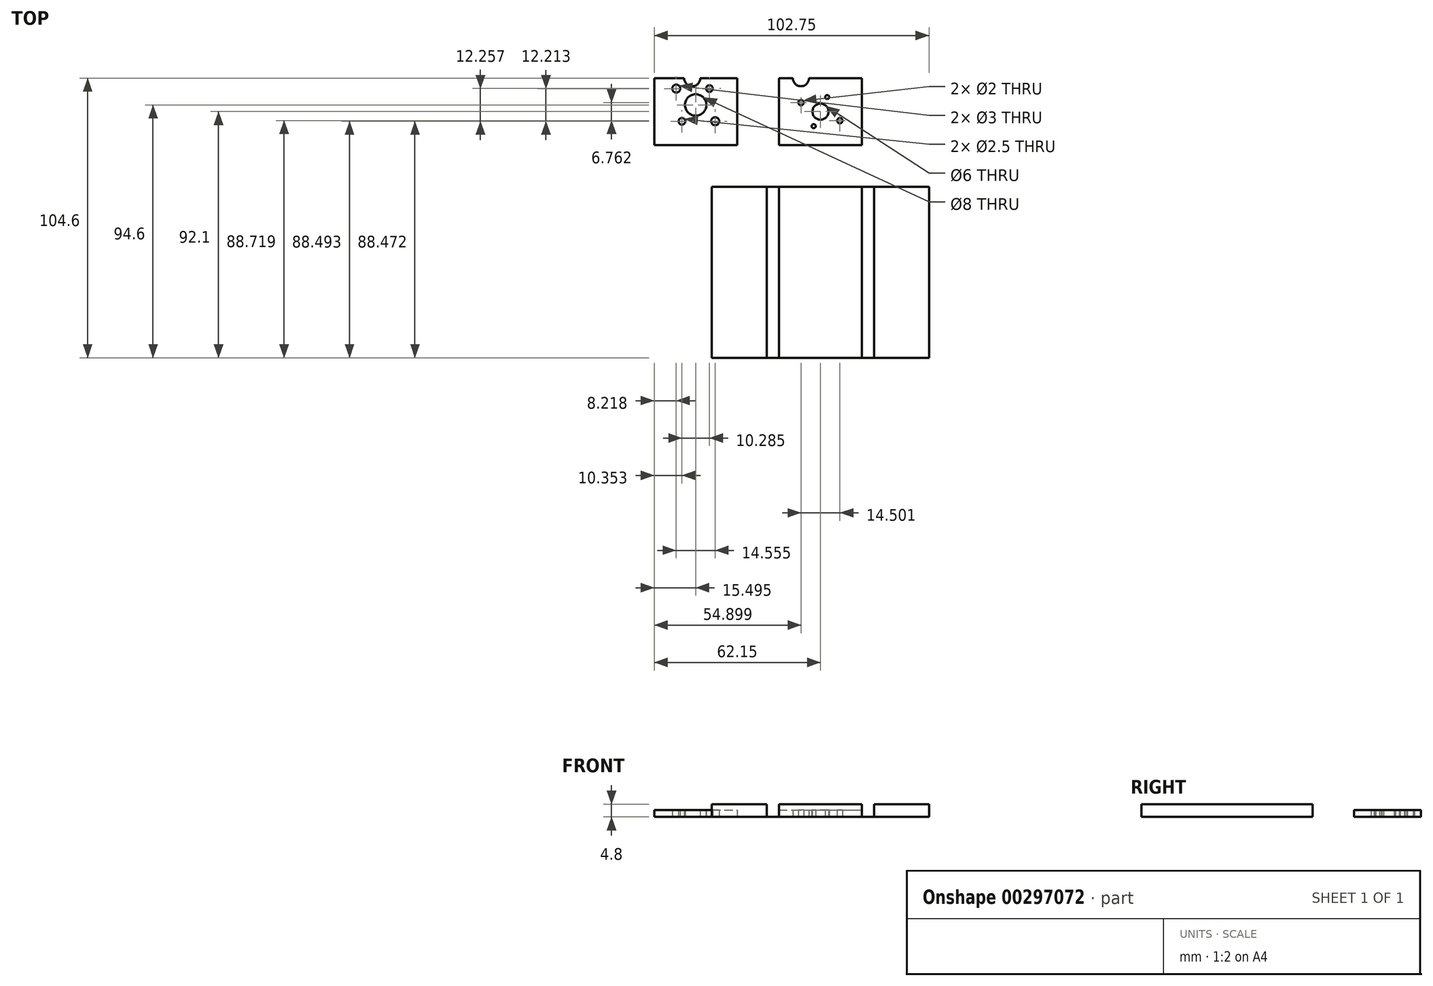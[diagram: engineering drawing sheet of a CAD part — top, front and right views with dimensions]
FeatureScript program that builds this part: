
annotation { "Feature Type Name" : "Feature", "Feature Type Description" : "" }
export const myFeature = defineFeature(function(context is Context, id is Id, definition is map)
    precondition{}
    {
        {
            assignVariable(context, id + "F0", {"name" : "foam_th", "lengthValue" : 4.7 * mm, "variableType" : VariableType.LENGTH});
        }
        {
            var Q0;
            Q0=qCreatedBy(makeId("Top.planeOp"),FACE);
            var sketch = newSketch(context, id + "F1", { "sketchPlane" : qUnion([Q0])});
            skLineSegment(sketch, "E0.bottom", {"start": v(0, 0) * mm, "end": v(31, 0) * mm});
            skLineSegment(sketch, "E0.top", {"start": v(0, 25) * mm, "end": v(5.2, 25) * mm});
            skLineSegment(sketch, "E0.left", {"start": v(0, 0) * mm, "end": v(0, 25) * mm});
            skLineSegment(sketch, "E0.right", {"start": v(31, 0) * mm, "end": v(31, 25) * mm});
            skPoint(sketch, "E1", {"position": v(15.5, 12.5) * mm});
            skLineSegment(sketch, "E2.bottom", {"start": v(25.29, 14.56) * mm, "end": v(10.79, 21.32) * mm, "construction": true});
            skLineSegment(sketch, "E2.top", {"start": v(20.21, 3.68) * mm, "end": v(5.71, 10.44) * mm, "construction": true});
            skLineSegment(sketch, "E2.left", {"start": v(25.29, 14.56) * mm, "end": v(20.21, 3.68) * mm, "construction": true});
            skLineSegment(sketch, "E2.right", {"start": v(10.79, 21.32) * mm, "end": v(5.71, 10.44) * mm, "construction": true});
            skCircle(sketch, "E3", {"center": v(18.04, 17.94) * mm, "radius": 0.75 * mm});
            skCircle(sketch, "E4", {"center": v(22.75, 9.12) * mm, "radius": 1 * mm});
            skCircle(sketch, "E5", {"center": v(8.25, 15.88) * mm, "radius": 1 * mm});
            skCircle(sketch, "E6", {"center": v(12.96, 7.06) * mm, "radius": 0.75 * mm});
            skCircle(sketch, "E7", {"center": v(15.5, 12.5) * mm, "radius": 3 * mm});
            skLineSegment(sketch, "E8.0", {"start": v(4.7, 4.7) * mm, "end": v(4.7, 25) * mm, "construction": true});
            skLineSegment(sketch, "E8.1", {"start": v(4.7, 4.7) * mm, "end": v(26.3, 4.7) * mm, "construction": true});
            skLineSegment(sketch, "E8.2", {"start": v(26.3, 4.7) * mm, "end": v(26.3, 25) * mm, "construction": true});
            skArc(sketch, "E9", {"start": v(5.2, 25) * mm, "mid": v(8.2, 22) * mm, "end": v(11.2, 25) * mm});
            skLineSegment(sketch, "E10.trimOffspring", {"start": v(26.3, 25) * mm, "end": v(31, 25) * mm});
            skCircle(sketch, "E11", {"center": v(18.04, 17.94) * mm, "radius": 1.9 * mm, "construction": true});
            skCircle(sketch, "E12", {"center": v(8.25, 15.88) * mm, "radius": 1.9 * mm, "construction": true});
            skCircle(sketch, "E13", {"center": v(22.75, 9.12) * mm, "radius": 1.9 * mm, "construction": true});
            skCircle(sketch, "E14", {"center": v(12.96, 7.06) * mm, "radius": 1.9 * mm, "construction": true});
            skLineSegment(sketch, "E15", {"start": v(10.79, 21.32) * mm, "end": v(20.21, 3.68) * mm, "construction": true});
            skLineSegment(sketch, "E16", {"start": v(15.5, 0) * mm, "end": v(15.5, 25) * mm, "construction": true});
            skLineSegment(sketch, "E17", {"start": v(26.3, 25) * mm, "end": v(11.2, 25) * mm});
            skCircle(sketch, "E18", {"center": v(15.5, 12.5) * mm, "radius": 11.5 * mm, "construction": true});
            skSolve(sketch);
        }
        {
            var Q0;
            Q0=qCreatedBy(makeId("Top.planeOp"),FACE);
            var sketch = newSketch(context, id + "F2", { "sketchPlane" : qUnion([Q0])});
            skLineSegment(sketch, "E19.bottom", {"start": v(-46.65, 0) * mm, "end": v(-15.65, 0) * mm});
            skLineSegment(sketch, "E19.top", {"start": v(-46.65, 25) * mm, "end": v(-35.45, 25) * mm});
            skLineSegment(sketch, "E19.left", {"start": v(-46.65, 0) * mm, "end": v(-46.65, 25) * mm});
            skLineSegment(sketch, "E19.right", {"start": v(-15.65, 0) * mm, "end": v(-15.65, 25) * mm});
            skPoint(sketch, "E20", {"position": v(-31.15, 15) * mm});
            skLineSegment(sketch, "E21.bottom", {"start": v(-33.3, 27.23) * mm, "end": v(-43.57, 14.98) * mm, "construction": true});
            skLineSegment(sketch, "E21.top", {"start": v(-18.74, 15.02) * mm, "end": v(-29.02, 2.77) * mm, "construction": true});
            skLineSegment(sketch, "E21.left", {"start": v(-33.3, 27.23) * mm, "end": v(-18.74, 15.02) * mm, "construction": true});
            skLineSegment(sketch, "E21.right", {"start": v(-43.57, 14.98) * mm, "end": v(-29.02, 2.77) * mm, "construction": true});
            skCircle(sketch, "E22", {"center": v(-38.43, 21.1) * mm, "radius": 1.5 * mm});
            skCircle(sketch, "E23", {"center": v(-26.01, 21.13) * mm, "radius": 1.25 * mm});
            skCircle(sketch, "E24", {"center": v(-36.3, 8.87) * mm, "radius": 1.25 * mm});
            skCircle(sketch, "E25", {"center": v(-23.88, 8.9) * mm, "radius": 1.5 * mm});
            skCircle(sketch, "E26", {"center": v(-31.15, 15) * mm, "radius": 4 * mm});
            skLineSegment(sketch, "E27.0", {"start": v(-41.95, 4.7) * mm, "end": v(-41.95, 25) * mm, "construction": true});
            skLineSegment(sketch, "E27.1", {"start": v(-41.95, 4.7) * mm, "end": v(-20.35, 4.7) * mm, "construction": true});
            skLineSegment(sketch, "E27.2", {"start": v(-20.35, 4.7) * mm, "end": v(-20.35, 25) * mm, "construction": true});
            skArc(sketch, "E28", {"start": v(-35.45, 25) * mm, "mid": v(-32.45, 22) * mm, "end": v(-29.45, 25) * mm});
            skLineSegment(sketch, "E29.trimOffspring", {"start": v(-20.35, 25) * mm, "end": v(-15.65, 25) * mm});
            skCircle(sketch, "E30", {"center": v(-38.43, 21.1) * mm, "radius": 2.75 * mm, "construction": true});
            skCircle(sketch, "E31", {"center": v(-36.3, 8.87) * mm, "radius": 2.75 * mm, "construction": true});
            skCircle(sketch, "E32", {"center": v(-26.01, 21.13) * mm, "radius": 2.75 * mm, "construction": true});
            skCircle(sketch, "E33", {"center": v(-23.88, 8.9) * mm, "radius": 2.75 * mm, "construction": true});
            skLineSegment(sketch, "E34", {"start": v(-43.57, 14.98) * mm, "end": v(-18.74, 15.02) * mm, "construction": true});
            skLineSegment(sketch, "E35", {"start": v(-31.15, 0) * mm, "end": v(-31.15, 25) * mm, "construction": true});
            skPoint(sketch, "E36", {"position": v(-31.15, 12.5) * mm});
            skLineSegment(sketch, "E37", {"start": v(-29.45, 25) * mm, "end": v(-20.35, 25) * mm});
            skCircle(sketch, "E38", {"center": v(-31.15, 15) * mm, "radius": 14.5 * mm, "construction": true});
            skSolve(sketch);
        }
        {
            var Q0;
            Q0=qCreatedBy(makeId("Top.planeOp"),FACE);
            var sketch = newSketch(context, id + "F3", { "sketchPlane" : qUnion([Q0])});
            skLineSegment(sketch, "E39.bottom", {"start": v(0, -15.6) * mm, "end": v(31, -15.6) * mm, "construction": true});
            skLineSegment(sketch, "E39.top", {"start": v(0, -79.6) * mm, "end": v(31, -79.6) * mm});
            skLineSegment(sketch, "E39.left", {"start": v(0, -15.6) * mm, "end": v(0, -79.6) * mm});
            skLineSegment(sketch, "E39.right", {"start": v(31, -15.6) * mm, "end": v(31, -79.6) * mm});
            skLineSegment(sketch, "E40.bottom", {"start": v(-4.6, -79.6) * mm, "end": v(-25.1, -79.6) * mm});
            skLineSegment(sketch, "E40.top", {"start": v(-4.6, -15.6) * mm, "end": v(-25.1, -15.6) * mm, "construction": true});
            skLineSegment(sketch, "E40.left", {"start": v(-4.6, -79.6) * mm, "end": v(-4.6, -15.6) * mm});
            skLineSegment(sketch, "E40.right", {"start": v(-25.1, -79.6) * mm, "end": v(-25.1, -15.6) * mm, "construction": true});
            skLineSegment(sketch, "E41.bottom", {"start": v(35.6, -79.6) * mm, "end": v(56.1, -79.6) * mm});
            skLineSegment(sketch, "E41.top", {"start": v(35.6, -15.6) * mm, "end": v(56.1, -15.6) * mm});
            skLineSegment(sketch, "E41.left", {"start": v(35.6, -79.6) * mm, "end": v(35.6, -15.6) * mm});
            skLineSegment(sketch, "E41.right", {"start": v(56.1, -79.6) * mm, "end": v(56.1, -15.6) * mm, "construction": true});
            skLineSegment(sketch, "E42", {"start": v(-4.6, -15.6) * mm, "end": v(0, -15.6) * mm, "construction": true});
            skLineSegment(sketch, "E43", {"start": v(31, -15.6) * mm, "end": v(35.6, -15.6) * mm});
            skLineSegment(sketch, "E44", {"start": v(31, -79.6) * mm, "end": v(35.6, -79.6) * mm});
            skLineSegment(sketch, "E45", {"start": v(-4.6, -79.6) * mm, "end": v(0, -79.6) * mm});
            skLineSegment(sketch, "E46", {"start": v(31, -15.6) * mm, "end": v(0, -15.6) * mm});
            skLineSegment(sketch, "E47", {"start": v(0, -15.6) * mm, "end": v(-4.6, -15.6) * mm});
            skLineSegment(sketch, "E48", {"start": v(-4.6, -15.6) * mm, "end": v(-25.1, -15.6) * mm});
            skLineSegment(sketch, "E49", {"start": v(-25.1, -15.6) * mm, "end": v(-25.1, -15.6) * mm, "construction": true});
            skLineSegment(sketch, "E50", {"start": v(-4.6, -15.6) * mm, "end": v(-4.6, -15.6) * mm});
            skLineSegment(sketch, "E51", {"start": v(0, -15.6) * mm, "end": v(0, -15.6) * mm});
            skLineSegment(sketch, "E52", {"start": v(56.1, -15.6) * mm, "end": v(56.09, -79.6) * mm});
            skLineSegment(sketch, "E53", {"start": v(-25.1, -15.6) * mm, "end": v(-25.09, -79.6) * mm});
            skLineSegment(sketch, "E54", {"start": v(-25.1, -15.6) * mm, "end": v(-25.1, -15.6) * mm});
            skSolve(sketch);
        }
        {
            var Q0;
            Q0=makeQuery(id+"F1.imprint","IMPRINT",FACE,{"disambiguationData":[TD([[makeQuery(id+"F1.imprint","IMPRINT",EDGE,{"derivedFrom":sQuery(id+"F1.wireOp",EDGE,"E0.bottom")}),1.0]])]});
            var Q1;
            Q1=makeQuery(id+"F2.imprint","IMPRINT",FACE,{"disambiguationData":[TD([[makeQuery(id+"F2.imprint","IMPRINT",EDGE,{"derivedFrom":sQuery(id+"F2.wireOp",EDGE,"E19.bottom")}),1.0]])]});
            extrude(context, id + "F4", {"entities" : qUnion([Q0, Q1]), "depth" : 2.5 * mm});
        }
        {
            var Q0;
            {var subQ1=sQuery(id+"F3.wireOp",EDGE,"E40.left");Q0=makeQuery(id+"F3.imprint","IMPRINT",FACE,{"disambiguationData":[TD([[makeQuery(id+"F3.imprint","IMPRINT",EDGE,{"derivedFrom":subQ1}),1.0]])]});}
            var Q1;
            Q1=makeQuery(id+"F3.imprint","IMPRINT",FACE,{"disambiguationData":[TD([[makeQuery(id+"F3.imprint","IMPRINT",EDGE,{"derivedFrom":sQuery(id+"F3.wireOp",EDGE,"E39.left")}),-1.0]])]});
            var Q2;
            Q2=makeQuery(id+"F3.imprint","IMPRINT",FACE,{"disambiguationData":[TD([[makeQuery(id+"F3.imprint","IMPRINT",EDGE,{"derivedFrom":sQuery(id+"F3.wireOp",EDGE,"E39.top")}),1.0]])]});
            var Q3;
            Q3=makeQuery(id+"F3.imprint","IMPRINT",FACE,{"disambiguationData":[TD([[makeQuery(id+"F3.imprint","IMPRINT",EDGE,{"derivedFrom":sQuery(id+"F3.wireOp",EDGE,"E39.right")}),1.0]])]});
            var Q4;
            Q4=makeQuery(id+"F3.imprint","IMPRINT",FACE,{"disambiguationData":[TD([[makeQuery(id+"F3.imprint","IMPRINT",EDGE,{"derivedFrom":sQuery(id+"F3.wireOp",EDGE,"E41.top")}),-1.0]])]});
            extrude(context, id + "F5", {"entities" : qUnion([Q0, Q1, Q2, Q3, Q4]), "oppositeDirection" : true, "depth" : 0.1 * mm});
        }
        {
            var Q0;
            {var subQ1=sQuery(id+"F3.wireOp",EDGE,"E40.left");Q0=makeQuery(id+"F3.imprint","IMPRINT",FACE,{"disambiguationData":[TD([[makeQuery(id+"F3.imprint","IMPRINT",EDGE,{"derivedFrom":subQ1}),1.0]])]});}
            var Q1;
            Q1=makeQuery(id+"F3.imprint","IMPRINT",FACE,{"disambiguationData":[TD([[makeQuery(id+"F3.imprint","IMPRINT",EDGE,{"derivedFrom":sQuery(id+"F3.wireOp",EDGE,"E39.top")}),1.0]])]});
            var Q2;
            Q2=makeQuery(id+"F3.imprint","IMPRINT",FACE,{"disambiguationData":[TD([[makeQuery(id+"F3.imprint","IMPRINT",EDGE,{"derivedFrom":sQuery(id+"F3.wireOp",EDGE,"E41.top")}),-1.0]])]});
            extrude(context, id + "F6", {"entities" : qUnion([Q0, Q1, Q2]), "operationType" : NewBodyOperationType.ADD, "depth" : getVariable(context, 'foam_th')});
        }
    });
